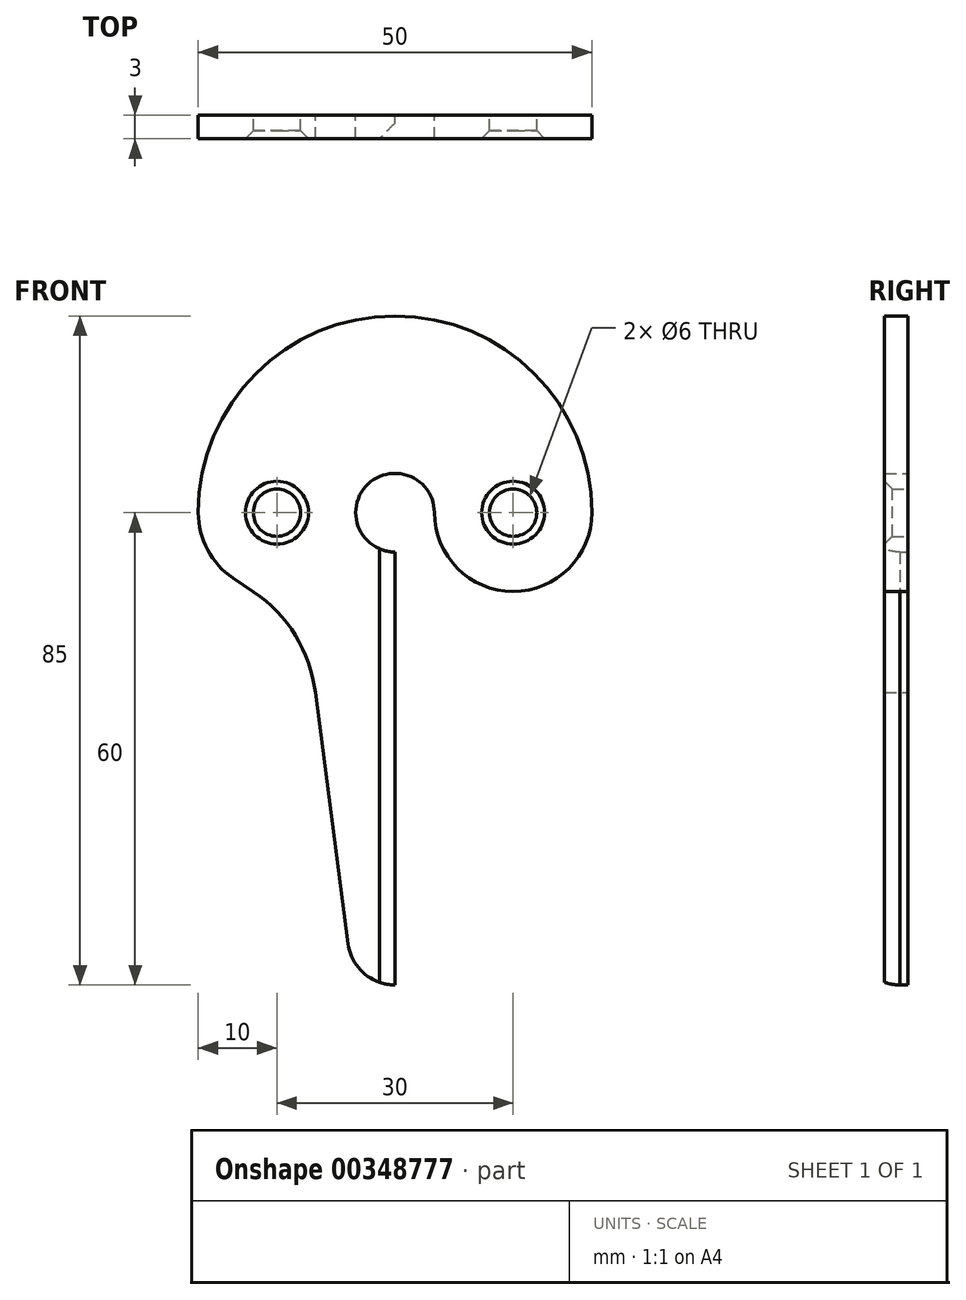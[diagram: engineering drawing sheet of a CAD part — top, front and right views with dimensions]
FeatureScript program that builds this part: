
annotation { "Feature Type Name" : "Feature", "Feature Type Description" : "" }
export const myFeature = defineFeature(function(context is Context, id is Id, definition is map)
    precondition{}
    {
        {
            var Q0;
            Q0=qCreatedBy(makeId("Front.planeOp"),FACE);
            var sketch = newSketch(context, id + "F0", { "sketchPlane" : qUnion([Q0])});
            skArc(sketch, "E0", {"start": v(25, 0) * mm, "mid": v(0, 25) * mm, "end": v(-25, 0) * mm});
            skArc(sketch, "E1", {"start": v(5, 0) * mm, "mid": v(-3.54, 3.54) * mm, "end": v(0, -5) * mm});
            skPoint(sketch, "E2", {"position": v(15, 0) * mm});
            skCircle(sketch, "E3", {"center": v(15, 0) * mm, "radius": 3 * mm});
            skArc(sketch, "E4", {"start": v(5, 0) * mm, "mid": v(15, -10) * mm, "end": v(25, 0) * mm});
            skPoint(sketch, "E5", {"position": v(0, -54) * mm});
            skPoint(sketch, "E6", {"position": v(-28, -25) * mm});
            skPoint(sketch, "E7.MirrorP", {"position": v(-15, 0) * mm});
            skCircle(sketch, "E8.MirrorC", {"center": v(-15, 0) * mm, "radius": 3 * mm});
            skArc(sketch, "E9.MirrorC", {"start": v(-20.58, -8.3) * mm, "mid": v(-23.83, -4.7) * mm, "end": v(-25, 0) * mm});
            skArc(sketch, "E10", {"start": v(-10.13, -22.86) * mm, "mid": v(-12.65, -15.6) * mm, "end": v(-17.96, -10.06) * mm});
            skLineSegment(sketch, "E11", {"start": v(0, -5) * mm, "end": v(0, -57) * mm});
            skLineSegment(sketch, "E12", {"start": v(-10.02, -22.9) * mm, "end": v(-10.43, -21.07) * mm});
            skArc(sketch, "E13.trimOffspring", {"start": v(-10.13, -22.86) * mm, "mid": v(-10.08, -22.88) * mm, "end": v(-10.02, -22.9) * mm});
            skLineSegment(sketch, "E14", {"start": v(-17.96, -10.06) * mm, "end": v(-20.58, -8.3) * mm});
            skArc(sketch, "E15", {"start": v(-5.95, -54.78) * mm, "mid": v(-3.96, -58.5) * mm, "end": v(0, -60) * mm});
            skLineSegment(sketch, "E16", {"start": v(0, -57) * mm, "end": v(0, -60) * mm});
            skLineSegment(sketch, "E17", {"start": v(-5.95, -54.78) * mm, "end": v(-10.15, -22.66) * mm});
            skSolve(sketch);
        }
        {
            var Q0;
            Q0 = qSketchRegion(id + "F0", true);
            extrude(context, id + "F1", {"entities" : qUnion([Q0]), "depth" : 3 * mm});
        }
        {
            var Q0;
            Q0=makeQuery(id+"F1.opExtrude","CAP_EDGE",EDGE,{"disambiguationData":[OSD([sQuery(id+"F0.wireOp",EDGE,"E8.MirrorC")])],"isStart":false});
            var Q1;
            Q1=makeQuery(id+"F1.opExtrude","CAP_EDGE",EDGE,{"disambiguationData":[OSD([sQuery(id+"F0.wireOp",EDGE,"E3")])],"isStart":false});
            chamfer(context, id + "F2", {"entities" : qUnion([Q0, Q1]), "width" : 1 * mm, "tangentPropagation" : true});
        }
        {
            var Q0;
            Q0=makeQuery(id+"F1.opExtrude","CAP_EDGE",EDGE,{"disambiguationData":[OSD([sQuery(id+"F0.wireOp",EDGE,"E11")])],"isStart":false});
            chamfer(context, id + "F3", {"entities" : qUnion([Q0]), "width" : 2 * mm, "tangentPropagation" : true});
        }
    });
